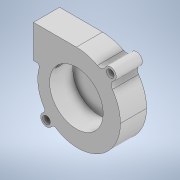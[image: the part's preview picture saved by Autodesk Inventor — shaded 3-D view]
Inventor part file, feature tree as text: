
AUTODESK INVENTOR PART (.ipt)
format: ipt  version: 2022 (Build 260153070, 153G)  size: 176,640 bytes
history: native  units: mm
features: extrude x3, sketch x3
ambient origin geometry x8: Origin, YZ Plane, XZ Plane, XY Plane, X Axis, Y Axis, Z Axis, Center Point
bodies: Solid1 (feature_tree)
feature tree (6):
  extrude  "Extrusion1"  Depth=19.7mm
  extrude  "Extrusion2"  Depth=17.8mm
  extrude  "Extrusion3"  Depth=13.9mm
  sketch  "Sketch1"  dims[d1=25.6mm d2=19.7mm]
  sketch  "Sketch2"  dims[d6=4.5mm d8=17.8mm]
  sketch  "Sketch3"  dims[d9=26.3mm d10=51.8mm d11=20.3mm d12=1.5mm d13=4.5mm d14=22.8mm d15=20.3mm d16=2.0mm d18=90.0deg d19=90.0deg d20=1.25mm d21=1.25mm d22=90.0deg d23=90.0deg d24=15.6mm d25=0.0mm d26=12.6mm d27=17.1mm d28=1.7mm d29=1.45mm d30=15.6mm d31=0.0mm d32=32.0mm d33=13.9mm d34=0.0mm]
